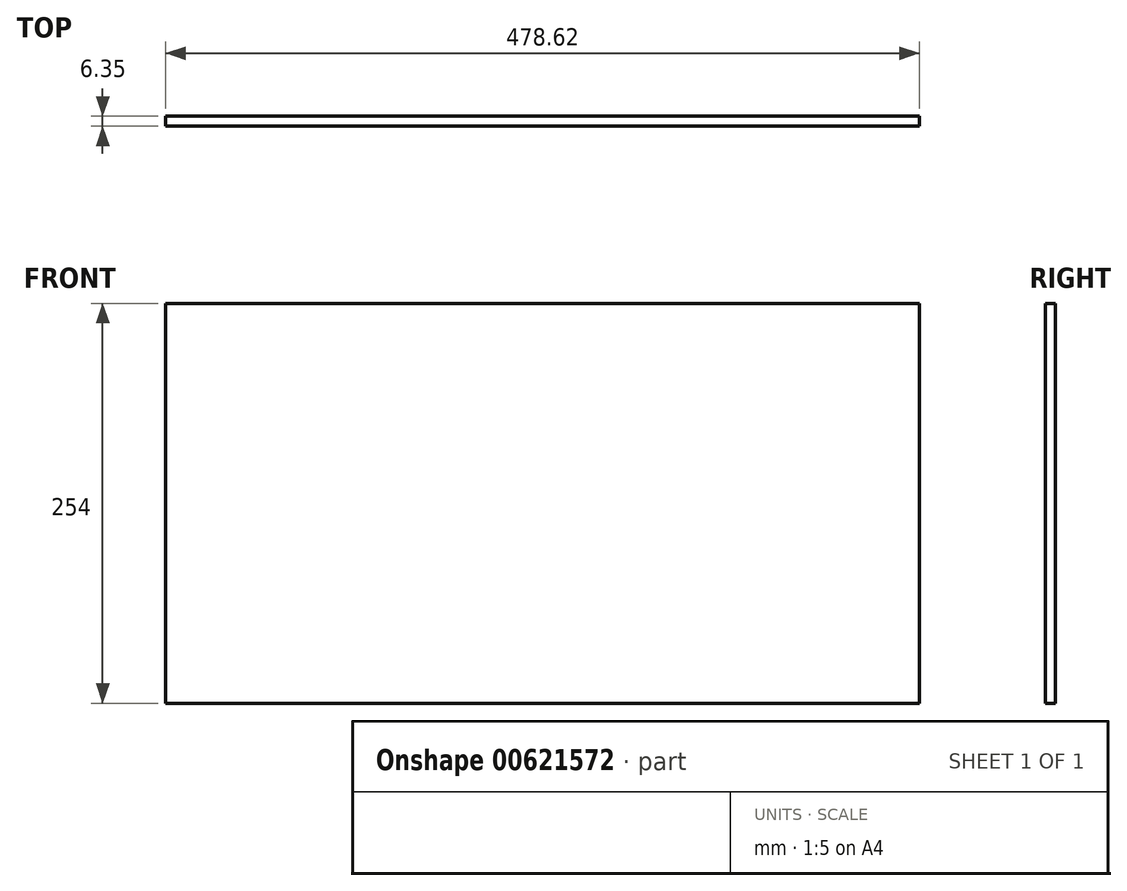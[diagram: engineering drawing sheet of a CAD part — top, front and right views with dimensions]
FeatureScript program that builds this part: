
annotation { "Feature Type Name" : "Feature", "Feature Type Description" : "" }
export const myFeature = defineFeature(function(context is Context, id is Id, definition is map)
    precondition{}
    {
        {
            var Q0;
            Q0=qCreatedBy(makeId("Front.planeOp"),FACE);
            var sketch = newSketch(context, id + "F0", { "sketchPlane" : qUnion([Q0])});
            skLineSegment(sketch, "E0.bottom", {"start": v(239.3, 127) * mm, "end": v(-239.3, 127) * mm});
            skLineSegment(sketch, "E0.top", {"start": v(239.3, -127) * mm, "end": v(-239.3, -127) * mm});
            skLineSegment(sketch, "E0.left", {"start": v(239.3, 127) * mm, "end": v(239.3, -127) * mm});
            skLineSegment(sketch, "E0.right", {"start": v(-239.3, 127) * mm, "end": v(-239.3, -127) * mm});
            skPoint(sketch, "E0.middle", {"position": v(0, 0) * mm});
            skSolve(sketch);
        }
        {
            var Q0;
            Q0 = qSketchRegion(id + "F0", true);
            extrude(context, id + "F1", {"entities" : qUnion([Q0]), "depth" : 6.35 * mm, "offsetDistance" : 25.4 * mm});
        }
    });
